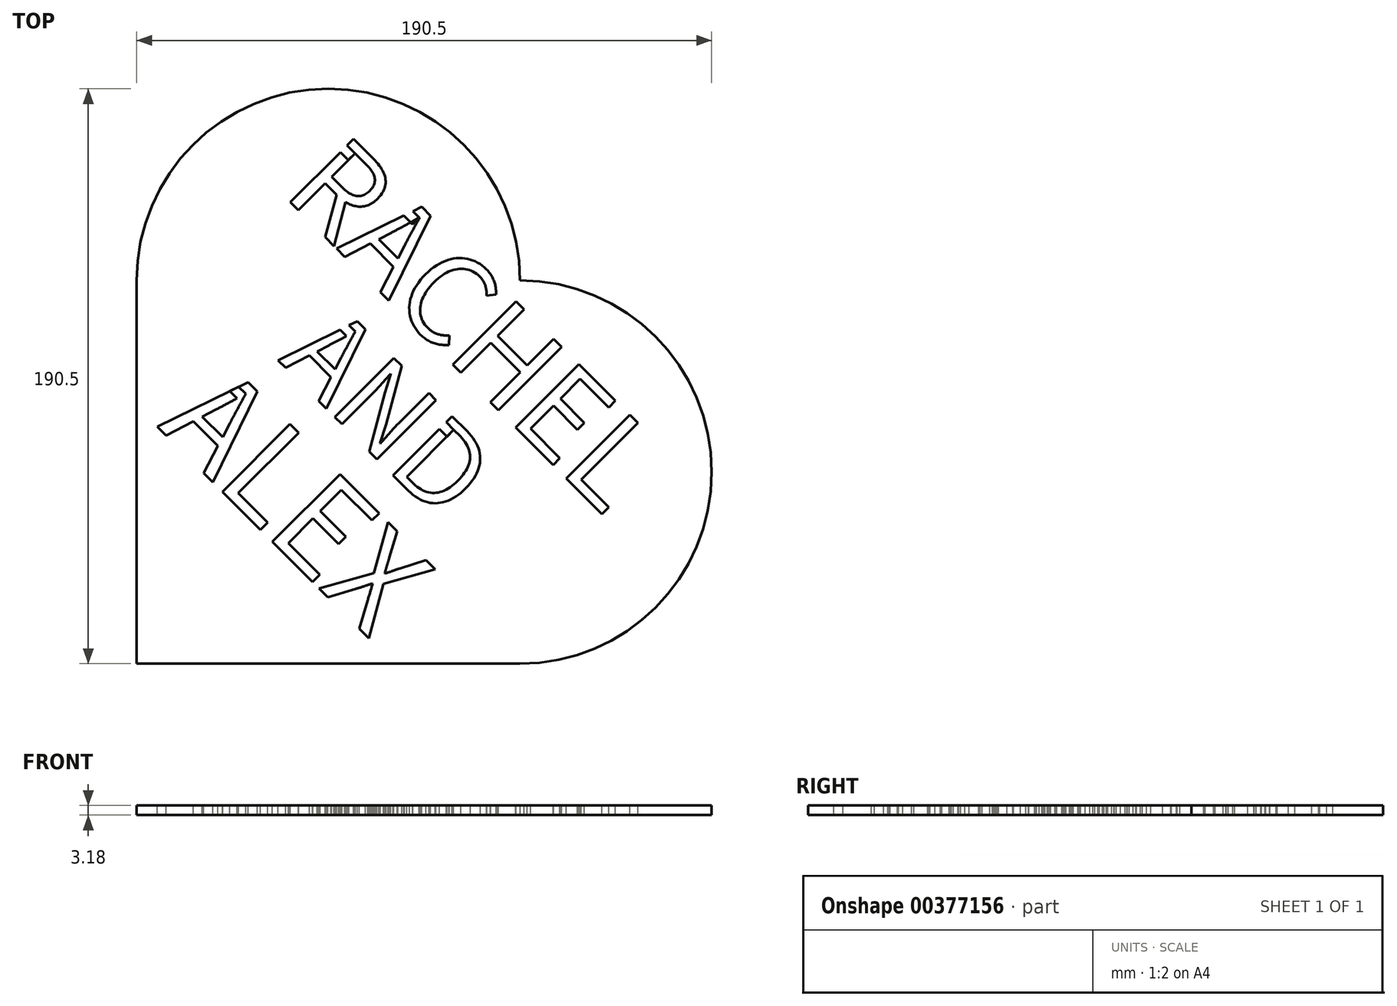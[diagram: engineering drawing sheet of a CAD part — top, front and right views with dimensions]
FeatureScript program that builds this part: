
annotation { "Feature Type Name" : "Feature", "Feature Type Description" : "" }
export const myFeature = defineFeature(function(context is Context, id is Id, definition is map)
    precondition{}
    {
        {
            var Q0;
            Q0=qCreatedBy(makeId("Top.planeOp"),FACE);
            var sketch = newSketch(context, id + "F0", { "sketchPlane" : qUnion([Q0])});
            skLineSegment(sketch, "E0.top", {"start": v(-158.75, -31.75) * mm, "end": v(-31.75, -31.75) * mm});
            skLineSegment(sketch, "E0.left", {"start": v(-158.75, 95.25) * mm, "end": v(-158.75, -31.75) * mm});
            skPoint(sketch, "E0.middle", {"position": v(-95.25, 31.75) * mm});
            skArc(sketch, "E1", {"start": v(-31.75, 95.25) * mm, "mid": v(-95.25, 158.75) * mm, "end": v(-158.75, 95.25) * mm});
            skArc(sketch, "E2", {"start": v(-31.75, -31.75) * mm, "mid": v(31.75, 31.75) * mm, "end": v(-31.75, 95.25) * mm});
            skPoint(sketch, "E3.orphan", {"position": v(-31.75, 95.25) * mm});
            skSolve(sketch);
        }
        {
            var Q0;
            Q0 = qSketchRegion(id + "F0", true);
            extrude(context, id + "F1", {"entities" : qUnion([Q0]), "depth" : 3.17 * mm});
        }
        {
            var Q0;
            Q0=makeQuery(id+"F1.opExtrude","CAP_FACE",FACE,{"disambiguationData":[OSD([sQuery(id+"F0.wireOp",EDGE,"E0.top"),sQuery(id+"F0.wireOp",EDGE,"E0.left"),sQuery(id+"F0.wireOp",EDGE,"E1"),sQuery(id+"F0.wireOp",EDGE,"E2")])],"isStart":false});
            var sketch = newSketch(context, id + "F2", { "sketchPlane" : qUnion([Q0])});
            skText(sketch, "E4", { "text": "RACHEL", "fontName": "NotoSansCJKjp-Regular.otf"});
            skLineSegment(sketch, "E5", {"start": v(-31.75, 95.25) * mm, "end": v(-158.75, -31.75) * mm, "construction": true});
            skText(sketch, "E6", { "text": "AND\n", "fontName": "NotoSansCJKjp-Regular.otf"});
            skText(sketch, "E7", { "text": "ALEX", "fontName": "NotoSansCJKjp-Regular.otf"});
            const initialGuessF2  = {"E4": [-0.11073, 0.12403, 0.7071, -0.7071, 0.02915], "E6": [-0.11202, 0.06886, 0.7071, -0.7071, 0.02723], "E7": [-0.152, 0.04684, 0.7071, -0.7071, 0.03114]};
            skSetInitialGuess(sketch, initialGuessF2);
            skSolve(sketch);
        }
        {
            var Q0;
            Q0 = qSketchRegion(id + "F2", true);
            extrude(context, id + "F3", {"entities" : qUnion([Q0]), "operationType" : NewBodyOperationType.REMOVE, "endBound" : BoundingType.UP_TO_NEXT, "oppositeDirection" : true, "depth" : 25.4 * mm});
        }
        {
            var Q0;
            {var subQ0=sQuery(id+"F0.wireOp",EDGE,"E1");var subQ1=sQuery(id+"F0.wireOp",EDGE,"E0.left");var subQ2=sQuery(id+"F0.wireOp",EDGE,"E2");var subQ3=sQuery(id+"F0.wireOp",EDGE,"E0.top");Q0=makeQuery(id+"F3.boolean.opBoolean","SPLIT",FACE,{"disambiguationData":[TD([makeQuery(id+"F1.opExtrude","SWEPT_FACE",FACE,{"disambiguationData":[OSD([subQ3])]})])],"derivedFrom":makeQuery(id+"F1.opExtrude","CAP_FACE",FACE,{"disambiguationData":[OSD([subQ3,subQ1,subQ0,subQ2])],"isStart":false})});}
            var sketch = newSketch(context, id + "F4", { "sketchPlane" : qUnion([Q0])});
            skLineSegment(sketch, "E8", {"start": v(-86.37, 137.34) * mm, "end": v(-89.03, 140) * mm});
            skLineSegment(sketch, "E9", {"start": v(-89.03, 140) * mm, "end": v(-91.28, 137.76) * mm});
            skLineSegment(sketch, "E10", {"start": v(-91.28, 137.76) * mm, "end": v(-88.62, 135.1) * mm});
            skLineSegment(sketch, "E11", {"start": v(-88.62, 135.1) * mm, "end": v(-86.37, 137.34) * mm});
            skLineSegment(sketch, "E12", {"start": v(-88.37, 80.4) * mm, "end": v(-86.4, 78.43) * mm});
            skLineSegment(sketch, "E13", {"start": v(-91.38, 78.91) * mm, "end": v(-88.65, 76.19) * mm});
            skLineSegment(sketch, "E14", {"start": v(-91.38, 78.91) * mm, "end": v(-88.37, 80.4) * mm});
            skLineSegment(sketch, "E15", {"start": v(-56.22, 48.24) * mm, "end": v(-53.73, 45.75) * mm});
            skLineSegment(sketch, "E16", {"start": v(-58.46, 46) * mm, "end": v(-55.97, 43.5) * mm});
            skLineSegment(sketch, "E17", {"start": v(-124.95, 60.03) * mm, "end": v(-122.7, 57.79) * mm});
            skLineSegment(sketch, "E18", {"start": v(-122.7, 57.79) * mm, "end": v(-122.7, 57.79) * mm});
            skLineSegment(sketch, "E19", {"start": v(-58.46, 46) * mm, "end": v(-56.22, 48.24) * mm});
            skLineSegment(sketch, "E20", {"start": v(-53.73, 45.75) * mm, "end": v(-55.97, 43.5) * mm});
            skLineSegment(sketch, "E21", {"start": v(-127.96, 58.55) * mm, "end": v(-124.95, 55.54) * mm});
            skLineSegment(sketch, "E22", {"start": v(-127.96, 58.55) * mm, "end": v(-124.95, 60.03) * mm});
            skLineSegment(sketch, "E23", {"start": v(-124.95, 55.54) * mm, "end": v(-122.7, 57.79) * mm});
            skLineSegment(sketch, "E24", {"start": v(-67.24, 118.2) * mm, "end": v(-65.13, 116.1) * mm});
            skLineSegment(sketch, "E25", {"start": v(-70.24, 116.72) * mm, "end": v(-67.24, 118.2) * mm});
            skLineSegment(sketch, "E26", {"start": v(-67.38, 113.86) * mm, "end": v(-70.24, 116.72) * mm});
            skLineSegment(sketch, "E27", {"start": v(-65.13, 116.1) * mm, "end": v(-67.38, 113.86) * mm});
            skLineSegment(sketch, "E28", {"start": v(-86.4, 78.43) * mm, "end": v(-88.65, 76.19) * mm});
            skSolve(sketch);
        }
        {
            var Q0;
            Q0 = qSketchRegion(id + "F4", true);
            extrude(context, id + "F5", {"entities" : qUnion([Q0]), "operationType" : NewBodyOperationType.ADD, "oppositeDirection" : true, "depth" : 3.17 * mm});
        }
    });
